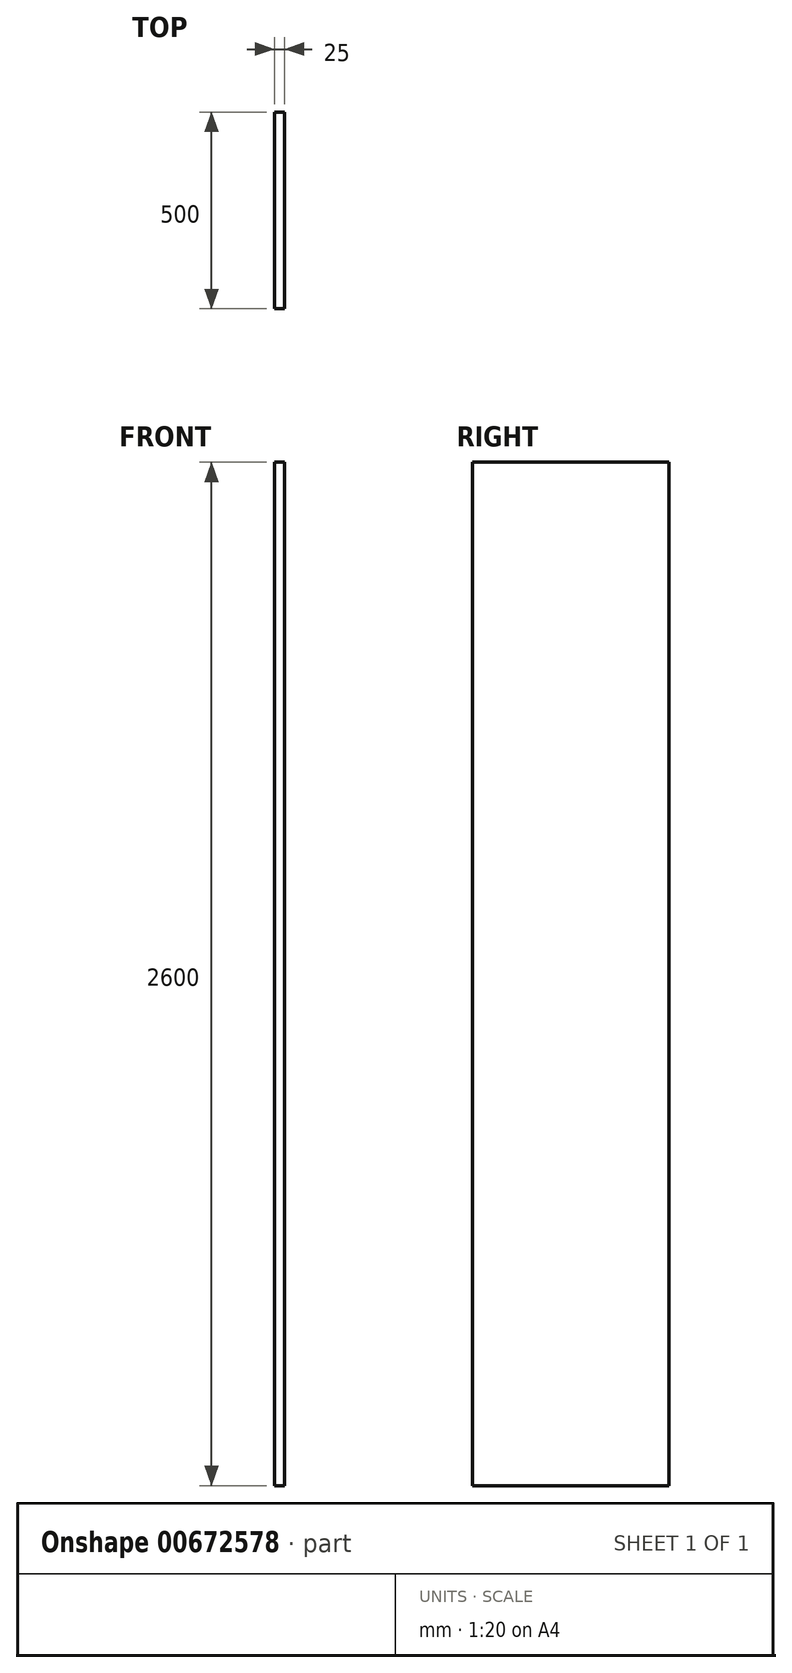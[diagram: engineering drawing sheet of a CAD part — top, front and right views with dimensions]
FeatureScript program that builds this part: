
annotation { "Feature Type Name" : "Feature", "Feature Type Description" : "" }
export const myFeature = defineFeature(function(context is Context, id is Id, definition is map)
    precondition{}
    {
        {
            var Q0;
            Q0=qCreatedBy(makeId("Right.planeOp"),FACE);
            var sketch = newSketch(context, id + "F0", { "sketchPlane" : qUnion([Q0])});
            skLineSegment(sketch, "E0.bottom", {"start": v(-250, 1300) * mm, "end": v(250, 1300) * mm});
            skLineSegment(sketch, "E0.top", {"start": v(-250, -1300) * mm, "end": v(250, -1300) * mm});
            skLineSegment(sketch, "E0.left", {"start": v(-250, 1300) * mm, "end": v(-250, -1300) * mm});
            skLineSegment(sketch, "E0.right", {"start": v(250, 1300) * mm, "end": v(250, -1300) * mm});
            skPoint(sketch, "E0.middle", {"position": v(0, 0) * mm});
            skSolve(sketch);
        }
        {
            var Q0;
            Q0=makeQuery(id+"F0.imprint","IMPRINT",FACE,{"disambiguationData":[TD([[makeQuery(id+"F0.imprint","IMPRINT",EDGE,{"derivedFrom":sQuery(id+"F0.wireOp",EDGE,"E0.bottom")}),-1.0]])]});
            extrude(context, id + "F1", {"entities" : qUnion([Q0]), "depth" : 25 * mm, "offsetDistance" : 25 * mm});
        }
    });
